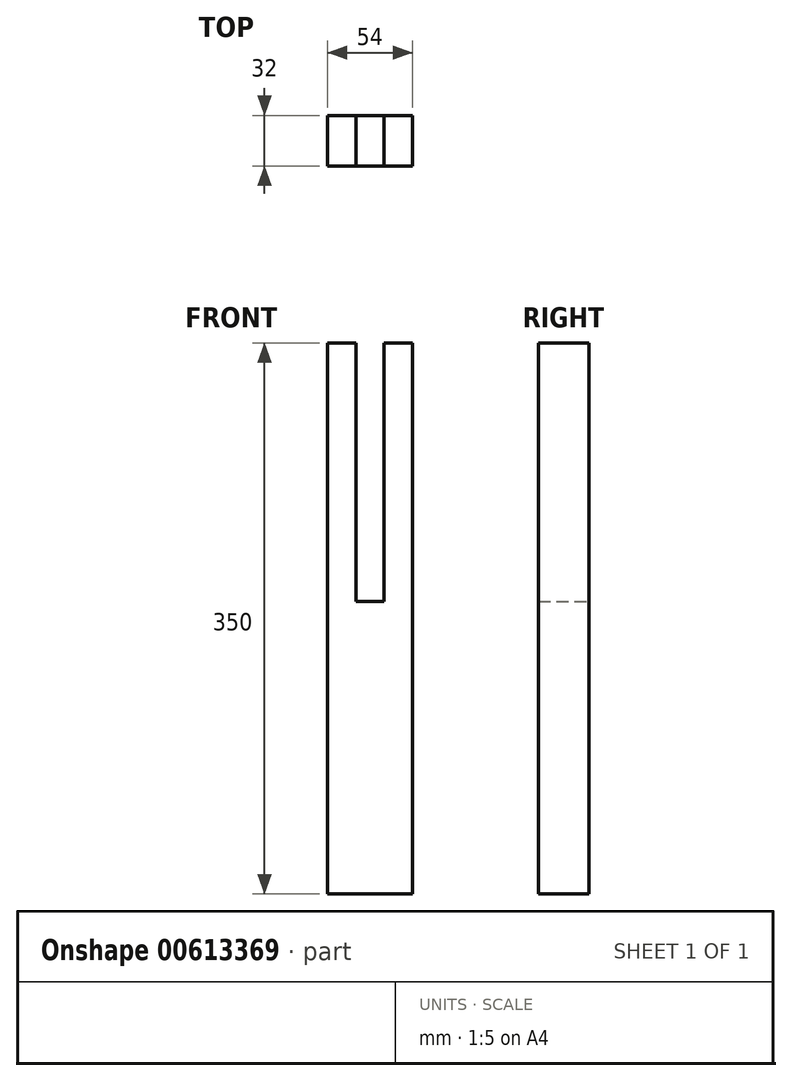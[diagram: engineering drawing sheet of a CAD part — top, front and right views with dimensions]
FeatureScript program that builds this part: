
annotation { "Feature Type Name" : "Feature", "Feature Type Description" : "" }
export const myFeature = defineFeature(function(context is Context, id is Id, definition is map)
    precondition{}
    {
        {
            var Q0;
            Q0=qCreatedBy(makeId("Front.planeOp"),FACE);
            var sketch = newSketch(context, id + "F0", { "sketchPlane" : qUnion([Q0])});
            skLineSegment(sketch, "E0", {"start": v(-27, 77.41) * mm, "end": v(-27, -272.59) * mm});
            skLineSegment(sketch, "E1", {"start": v(-27, -272.59) * mm, "end": v(-9, -272.59) * mm});
            skLineSegment(sketch, "E2", {"start": v(-27, 77.41) * mm, "end": v(-9, 77.41) * mm});
            skPoint(sketch, "E3.orphan", {"position": v(-9, 77) * mm});
            skPoint(sketch, "E4.orphan", {"position": v(7, 177) * mm});
            skLineSegment(sketch, "E5", {"start": v(-9, -86.66) * mm, "end": v(-9, 77.41) * mm});
            skLineSegment(sketch, "E6.MirrorCS", {"start": v(27, 77.41) * mm, "end": v(27, -272.59) * mm});
            skLineSegment(sketch, "E7.MirrorCS", {"start": v(9, -86.66) * mm, "end": v(9, 77.41) * mm});
            skLineSegment(sketch, "E8.MirrorCS", {"start": v(27, -272.59) * mm, "end": v(9, -272.59) * mm});
            skLineSegment(sketch, "E9.MirrorCS", {"start": v(27, 77.41) * mm, "end": v(9, 77.41) * mm});
            skLineSegment(sketch, "E10", {"start": v(-9, -86.66) * mm, "end": v(9, -86.66) * mm});
            skLineSegment(sketch, "E11", {"start": v(-9, -272.59) * mm, "end": v(9, -272.59) * mm});
            skPoint(sketch, "E12.MirrorCS.end.orphan", {"position": v(9, -86.66) * mm});
            skSolve(sketch);
        }
        {
            var Q0;
            Q0=makeQuery(id+"F0.imprint","IMPRINT",FACE,{"disambiguationData":[TD([[makeQuery(id+"F0.imprint","IMPRINT",EDGE,{"derivedFrom":sQuery(id+"F0.wireOp",EDGE,"E0")}),1.0]])]});
            var Q1;
            Q1=makeQuery(id+"F0.imprint","IMPRINT",FACE,{"disambiguationData":[TD([[makeQuery(id+"F0.imprint","IMPRINT",EDGE,{"derivedFrom":sQuery(id+"F0.wireOp",EDGE,"6123892c-3601-44bd-bc6b-f39b571c0fcb")}),-1.0]])]});
            var Q2;
            Q2=makeQuery(id+"F0.imprint","IMPRINT",FACE,{"disambiguationData":[TD([[makeQuery(id+"F0.imprint","IMPRINT",EDGE,{"derivedFrom":sQuery(id+"F0.wireOp",EDGE,"E6.MirrorCS")}),-1.0]])]});
            extrude(context, id + "F1", {"entities" : qUnion([Q0, Q1, Q2]), "depth" : 16 * mm, "offsetDistance" : 25 * mm, "hasSecondDirection" : true, "secondDirectionOppositeDirection" : true, "secondDirectionDepth" : 16 * mm});
        }
    });
